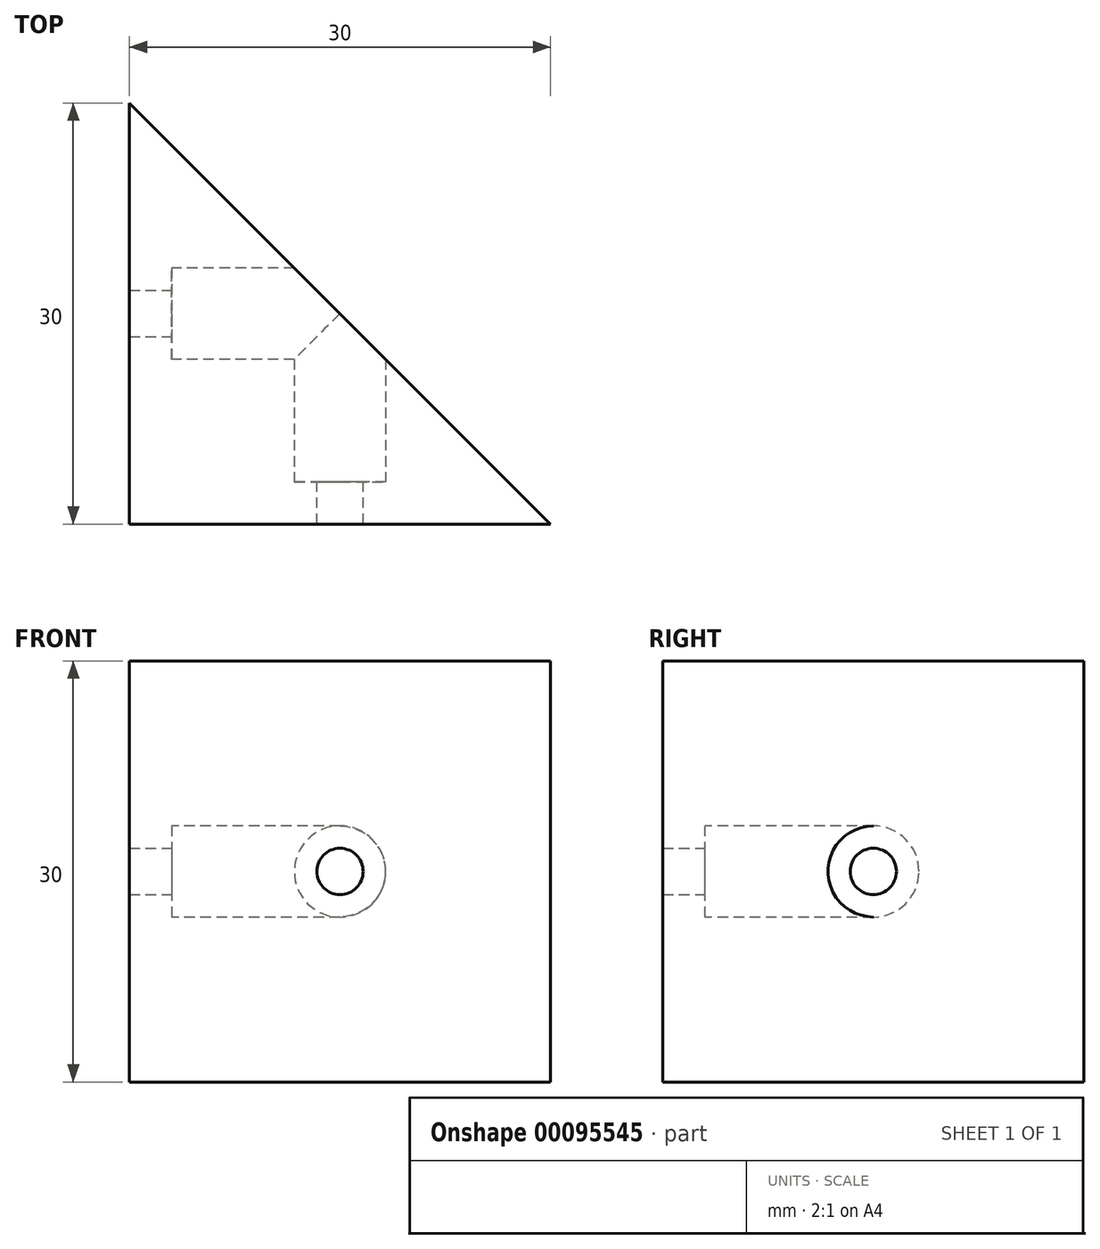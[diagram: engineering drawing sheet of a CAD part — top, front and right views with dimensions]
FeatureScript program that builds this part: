
annotation { "Feature Type Name" : "Feature", "Feature Type Description" : "" }
export const myFeature = defineFeature(function(context is Context, id is Id, definition is map)
    precondition{}
    {
        {
            assignVariable(context, id + "F0", {"name" : "c", "anyValue" : 30});
        }
        {
            var Q0;
            Q0=qCreatedBy(makeId("Top.planeOp"),FACE);
            var sketch = newSketch(context, id + "F1", { "sketchPlane" : qUnion([Q0])});
            skLineSegment(sketch, "E0.top", {"start": v(15, -15) * mm, "end": v(-15, -15) * mm});
            skLineSegment(sketch, "E0.right", {"start": v(-15, 15) * mm, "end": v(-15, -15) * mm});
            skPoint(sketch, "E0.middle", {"position": v(0, 0) * mm});
            skLineSegment(sketch, "E1", {"start": v(-15, 15) * mm, "end": v(15, -15) * mm});
            skSolve(sketch);
        }
        {
            var Q0;
            Q0 = qSketchRegion(id + "F1", true);
            extrude(context, id + "F2", {"entities" : qUnion([Q0]), "depth" : (getVariable(context, 'c')) * mm});
        }
        {
            var Q0;
            Q0=makeQuery(id+"F2.opExtrude","SWEPT_FACE",FACE,{"disambiguationData":[OSD([sQuery(id+"F1.wireOp",EDGE,"E0.right")])]});
            cPlane(context, id + "F3", {"entities" : qUnion([Q0]), "cplaneType" : CPlaneType.OFFSET, "offset" : 3 * mm, "oppositeDirection" : true, "width" : 150 * mm, "height" : 150 * mm});
        }
        {
            var Q0;
            Q0=qCreatedBy(id+"F3.planeOp",FACE);
            var sketch = newSketch(context, id + "F4", { "sketchPlane" : qUnion([Q0])});
            skCircle(sketch, "E2", {"center": v(0, 15) * mm, "radius": 3.25 * mm});
            skPoint(sketch, "E3", {"position": v(15, 15) * mm});
            skSolve(sketch);
        }
        {
            var Q0;
            Q0 = qSketchRegion(id + "F4", true);
            extrude(context, id + "F5", {"entities" : qUnion([Q0]), "operationType" : NewBodyOperationType.REMOVE, "endBound" : BoundingType.THROUGH_ALL, "oppositeDirection" : true, "depth" : 25 * mm});
        }
        {
            var Q0;
            Q0=qCreatedBy(id+"F3.planeOp",FACE);
            var sketch = newSketch(context, id + "F6", { "sketchPlane" : qUnion([Q0])});
            skPoint(sketch, "E4.0", {"position": v(0, 15) * mm});
            skCircle(sketch, "E5", {"center": v(0, 15) * mm, "radius": 1.65 * mm});
            skSolve(sketch);
        }
        {
            var Q0;
            Q0 = qSketchRegion(id + "F6", true);
            extrude(context, id + "F7", {"entities" : qUnion([Q0]), "operationType" : NewBodyOperationType.REMOVE, "endBound" : BoundingType.THROUGH_ALL, "depth" : 25 * mm});
        }
        {
            var Q0;
            Q0=makeQuery(id+"F2.opExtrude","SWEPT_FACE",FACE,{"disambiguationData":[OSD([sQuery(id+"F1.wireOp",EDGE,"E0.top")])]});
            cPlane(context, id + "F8", {"entities" : qUnion([Q0]), "cplaneType" : CPlaneType.OFFSET, "offset" : 3 * mm, "oppositeDirection" : true, "width" : 150 * mm, "height" : 150 * mm});
        }
        {
            var Q0;
            Q0=qCreatedBy(id+"F8.planeOp",FACE);
            var sketch = newSketch(context, id + "F9", { "sketchPlane" : qUnion([Q0])});
            skCircle(sketch, "E6", {"center": v(0, 15) * mm, "radius": 3.25 * mm});
            skPoint(sketch, "E7", {"position": v(15, 15) * mm});
            skSolve(sketch);
        }
        {
            var Q0;
            Q0 = qSketchRegion(id + "F9", true);
            extrude(context, id + "F10", {"entities" : qUnion([Q0]), "operationType" : NewBodyOperationType.REMOVE, "endBound" : BoundingType.THROUGH_ALL, "oppositeDirection" : true, "depth" : 25 * mm});
        }
        {
            var Q0;
            Q0=qCreatedBy(id+"F8.planeOp",FACE);
            var sketch = newSketch(context, id + "F11", { "sketchPlane" : qUnion([Q0])});
            skPoint(sketch, "E8.0", {"position": v(0, 15) * mm});
            skCircle(sketch, "E9", {"center": v(0, 15) * mm, "radius": 1.65 * mm});
            skSolve(sketch);
        }
        {
            var Q0;
            Q0 = qSketchRegion(id + "F11", true);
            extrude(context, id + "F12", {"entities" : qUnion([Q0]), "operationType" : NewBodyOperationType.REMOVE, "depth" : 25 * mm});
        }
    });
